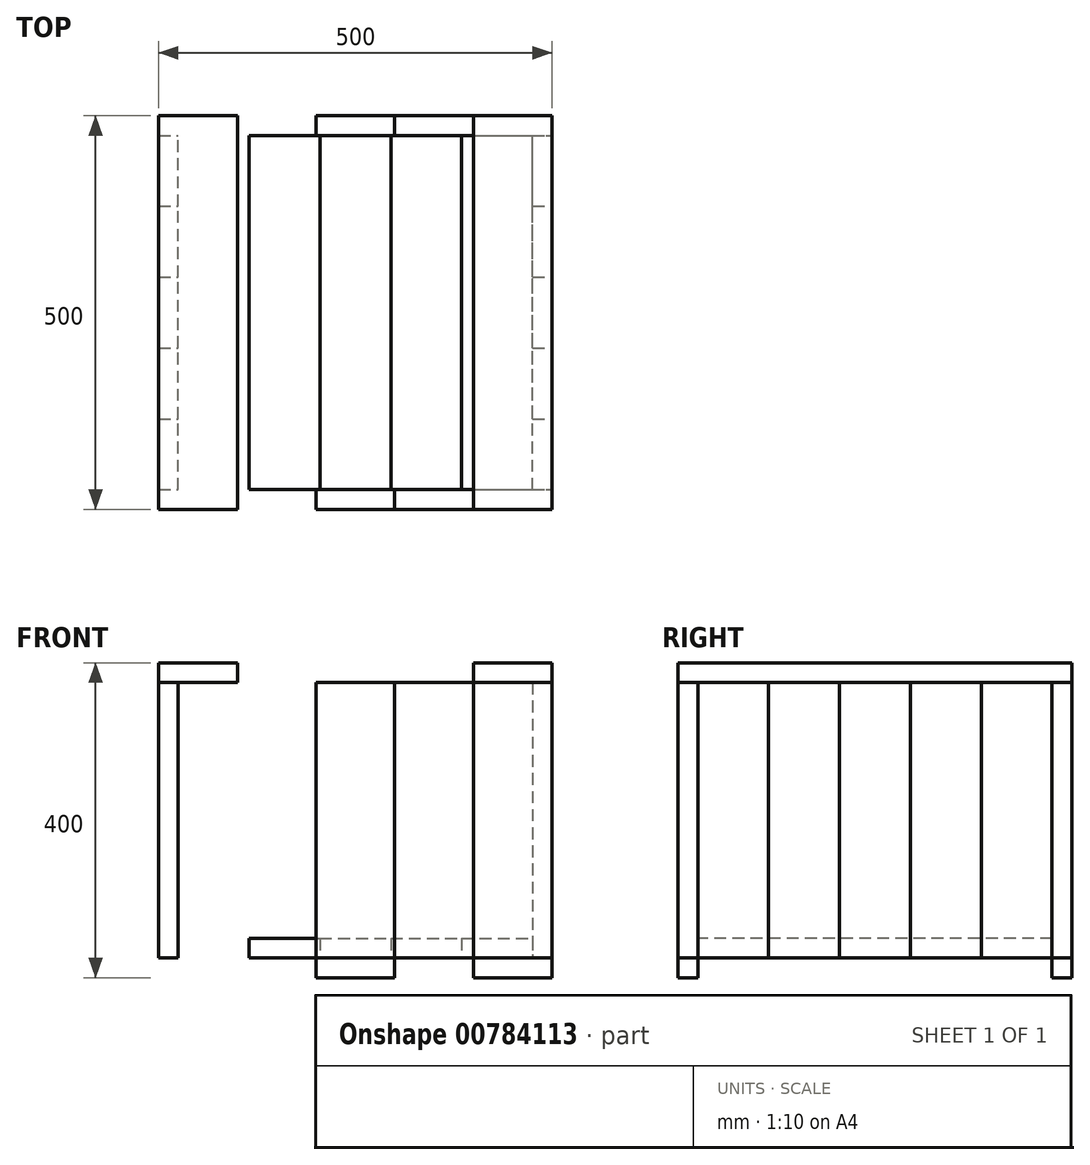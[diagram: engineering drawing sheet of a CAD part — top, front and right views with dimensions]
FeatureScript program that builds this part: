
annotation { "Feature Type Name" : "Feature", "Feature Type Description" : "" }
export const myFeature = defineFeature(function(context is Context, id is Id, definition is map)
    precondition{}
    {
        {
            var Q0;
            Q0=qCreatedBy(makeId("Top.planeOp"),FACE);
            var sketch = newSketch(context, id + "F0", { "sketchPlane" : qUnion([Q0])});
            skLineSegment(sketch, "E0.bottom", {"start": v(0, 0) * mm, "end": v(450, 0) * mm});
            skLineSegment(sketch, "E0.top", {"start": v(0, 450) * mm, "end": v(450, 450) * mm});
            skLineSegment(sketch, "E0.left", {"start": v(0, 0) * mm, "end": v(0, 450) * mm});
            skLineSegment(sketch, "E0.right", {"start": v(450, 0) * mm, "end": v(450, 450) * mm});
            skLineSegment(sketch, "E1.bottom", {"start": v(0, 450) * mm, "end": v(90, 450) * mm});
            skLineSegment(sketch, "E1.top", {"start": v(0, 0) * mm, "end": v(90, 0) * mm});
            skLineSegment(sketch, "E1.left", {"start": v(0, 450) * mm, "end": v(0, 0) * mm});
            skLineSegment(sketch, "E1.right", {"start": v(90, 450) * mm, "end": v(90, 0) * mm});
            skLineSegment(sketch, "E2.1.0.0", {"start": v(180, 450) * mm, "end": v(180, 0) * mm});
            skLineSegment(sketch, "E2.2.0.0", {"start": v(270, 450) * mm, "end": v(270, 0) * mm});
            skLineSegment(sketch, "E2.3.0.0", {"start": v(360, 450) * mm, "end": v(360, 0) * mm});
            skLineSegment(sketch, "E2.direction1", {"start": v(90, 0) * mm, "end": v(180, 0) * mm, "construction": true});
            skLineSegment(sketch, "E3.0", {"start": v(-25, 475) * mm, "end": v(475, 475) * mm});
            skLineSegment(sketch, "E3.1", {"start": v(-25, 475) * mm, "end": v(-25, -25) * mm});
            skLineSegment(sketch, "E3.2", {"start": v(-25, -25) * mm, "end": v(475, -25) * mm});
            skLineSegment(sketch, "E3.3", {"start": v(475, -25) * mm, "end": v(475, 475) * mm});
            skLineSegment(sketch, "E4.bottom", {"start": v(-25, -25) * mm, "end": v(75, -25) * mm});
            skLineSegment(sketch, "E4.top", {"start": v(-25, 0) * mm, "end": v(75, 0) * mm});
            skLineSegment(sketch, "E4.left", {"start": v(-25, -25) * mm, "end": v(-25, 0) * mm});
            skLineSegment(sketch, "E4.right", {"start": v(75, -25) * mm, "end": v(75, 0) * mm});
            skLineSegment(sketch, "E5.1.0.0", {"start": v(175, -25) * mm, "end": v(175, 0) * mm});
            skLineSegment(sketch, "E5.2.0.0", {"start": v(275, -25) * mm, "end": v(275, 0) * mm});
            skLineSegment(sketch, "E5.3.0.0", {"start": v(375, -25) * mm, "end": v(375, 0) * mm});
            skLineSegment(sketch, "E5.direction1", {"start": v(75, -25) * mm, "end": v(175, -25) * mm, "construction": true});
            skLineSegment(sketch, "E6", {"start": v(450, 0) * mm, "end": v(475, 0) * mm});
            skLineSegment(sketch, "E7", {"start": v(450, 90) * mm, "end": v(475, 90) * mm});
            skLineSegment(sketch, "E8.0.1.0", {"start": v(450, 180) * mm, "end": v(475, 180) * mm});
            skLineSegment(sketch, "E8.0.2.0", {"start": v(450, 270) * mm, "end": v(475, 270) * mm});
            skLineSegment(sketch, "E8.0.3.0", {"start": v(450, 360) * mm, "end": v(475, 360) * mm});
            skLineSegment(sketch, "E8.direction1", {"start": v(450, 90) * mm, "end": v(475, 90) * mm, "construction": true});
            skLineSegment(sketch, "E8.direction2", {"start": v(450, 90) * mm, "end": v(450, 180) * mm, "construction": true});
            skLineSegment(sketch, "E9", {"start": v(450, 450) * mm, "end": v(475, 450) * mm});
            skSolve(sketch);
        }
        {
            var Q0;
            Q0=makeQuery(id+"F0.imprint","IMPRINT",FACE,{"disambiguationData":[TD([[makeQuery(id+"F0.imprint","IMPRINT",EDGE,{"derivedFrom":sQuery(id+"F0.wireOp",EDGE,"E1.bottom")}),-1.0]])]});
            var Q1;
            {var subQ0=sQuery(id+"F0.wireOp",EDGE,"E2.1.0.0");Q1=makeQuery(id+"F0.imprint","IMPRINT",FACE,{"disambiguationData":[TD([[makeQuery(id+"F0.imprint","IMPRINT",EDGE,{"derivedFrom":subQ0}),1.0]])]});}
            var Q2;
            {var subQ0=sQuery(id+"F0.wireOp",EDGE,"E0.right");Q2=makeQuery(id+"F0.imprint","IMPRINT",FACE,{"disambiguationData":[TD([[makeQuery(id+"F0.imprint","IMPRINT",EDGE,{"derivedFrom":subQ0}),1.0]])]});}
            extrude(context, id + "F1", {"entities" : qUnion([Q0, Q1, Q2]), "depth" : 25 * mm, "offsetDistance" : 25 * mm});
        }
        {
            var Q0;
            {var subQ0=sQuery(id+"F0.wireOp",EDGE,"E1.right");Q0=makeQuery(id+"F0.imprint","IMPRINT",FACE,{"disambiguationData":[TD([[makeQuery(id+"F0.imprint","IMPRINT",EDGE,{"derivedFrom":subQ0}),1.0]])]});}
            var Q1;
            {var subQ0=sQuery(id+"F0.wireOp",EDGE,"E2.2.0.0");Q1=makeQuery(id+"F0.imprint","IMPRINT",FACE,{"disambiguationData":[TD([[makeQuery(id+"F0.imprint","IMPRINT",EDGE,{"derivedFrom":subQ0}),1.0]])]});}
            extrude(context, id + "F2", {"entities" : qUnion([Q0, Q1]), "depth" : 25 * mm, "offsetDistance" : 25 * mm});
        }
        {
            var Q0;
            Q0=makeQuery(id+"F0.imprint","IMPRINT",FACE,{"disambiguationData":[TD([[makeQuery(id+"F0.imprint","IMPRINT",EDGE,{"derivedFrom":sQuery(id+"F0.wireOp",EDGE,"E4.bottom")}),1.0]])]});
            var Q1;
            {var subQ3=sQuery(id+"F0.wireOp",EDGE,"E5.1.0.0");Q1=makeQuery(id+"F0.imprint","IMPRINT",FACE,{"disambiguationData":[TD([[makeQuery(id+"F0.imprint","IMPRINT",EDGE,{"derivedFrom":subQ3}),-1.0]])]});}
            var Q2;
            {var subQ4=sQuery(id+"F0.wireOp",EDGE,"E5.3.0.0");Q2=makeQuery(id+"F0.imprint","IMPRINT",FACE,{"disambiguationData":[TD([[makeQuery(id+"F0.imprint","IMPRINT",EDGE,{"derivedFrom":subQ4}),-1.0]])]});}
            extrude(context, id + "F3", {"entities" : qUnion([Q0, Q1, Q2]), "depth" : 350 * mm, "offsetDistance" : 25 * mm});
        }
        {
            var Q0;
            {var subQ3=sQuery(id+"F0.wireOp",EDGE,"E1.top");Q0=makeQuery(id+"F0.imprint","IMPRINT",FACE,{"disambiguationData":[TD([[makeQuery(id+"F0.imprint","IMPRINT",EDGE,{"derivedFrom":subQ3}),-1.0]])]});}
            var Q1;
            {var subQ0=sQuery(id+"F0.wireOp",EDGE,"E5.2.0.0");Q1=makeQuery(id+"F0.imprint","IMPRINT",FACE,{"disambiguationData":[TD([[makeQuery(id+"F0.imprint","IMPRINT",EDGE,{"derivedFrom":subQ0}),-1.0]])]});}
            extrude(context, id + "F4", {"entities" : qUnion([Q0, Q1]), "depth" : 350 * mm, "offsetDistance" : 25 * mm});
        }
        {
            var Q0;
            Q0=makeQuery(id+"F3.opExtrude","SWEPT_BODY",BODY,{"disambiguationData":[OSD([sQuery(id+"F0.wireOp",EDGE,"E4.bottom"),sQuery(id+"F0.wireOp",EDGE,"E4.top"),sQuery(id+"F0.wireOp",EDGE,"E4.left"),sQuery(id+"F0.wireOp",EDGE,"E4.right")])]});
            var Q1;
            Q1=makeQuery(id+"F4.opExtrude","SWEPT_BODY",BODY,{"disambiguationData":[OSD([sQuery(id+"F0.wireOp",EDGE,"E0.bottom"),sQuery(id+"F0.wireOp",EDGE,"E1.top"),sQuery(id+"F0.wireOp",EDGE,"E3.2"),sQuery(id+"F0.wireOp",EDGE,"E4.right"),sQuery(id+"F0.wireOp",EDGE,"E5.1.0.0")])]});
            var Q2;
            Q2=makeQuery(id+"F3.opExtrude","SWEPT_BODY",BODY,{"disambiguationData":[OSD([sQuery(id+"F0.wireOp",EDGE,"E0.bottom"),sQuery(id+"F0.wireOp",EDGE,"E3.2"),sQuery(id+"F0.wireOp",EDGE,"E5.1.0.0"),sQuery(id+"F0.wireOp",EDGE,"E5.2.0.0")])]});
            var Q3;
            Q3=makeQuery(id+"F4.opExtrude","SWEPT_BODY",BODY,{"disambiguationData":[OSD([sQuery(id+"F0.wireOp",EDGE,"E0.bottom"),sQuery(id+"F0.wireOp",EDGE,"E3.2"),sQuery(id+"F0.wireOp",EDGE,"E5.2.0.0"),sQuery(id+"F0.wireOp",EDGE,"E5.3.0.0")])]});
            var Q4;
            Q4=makeQuery(id+"F3.opExtrude","SWEPT_BODY",BODY,{"disambiguationData":[OSD([sQuery(id+"F0.wireOp",EDGE,"E0.bottom"),sQuery(id+"F0.wireOp",EDGE,"E3.2"),sQuery(id+"F0.wireOp",EDGE,"E3.3"),sQuery(id+"F0.wireOp",EDGE,"E5.3.0.0"),sQuery(id+"F0.wireOp",EDGE,"E6")])]});
            var Q5;
            Q5=makeQuery(id+"F3.opExtrude","SWEPT_FACE",FACE,{"disambiguationData":[OSD([sQuery(id+"F0.wireOp",EDGE,"E0.bottom")])]});
            transform(context, id + "F5", {"entities" : qUnion([Q0, Q1, Q2, Q3, Q4]), "transformType" : TransformType.TRANSLATION_DISTANCE, "transformDirection" : qUnion([Q5]), "distance" : 475 * mm, "makeCopy" : true});
        }
        {
            var Q0;
            Q0=makeQuery(id+"F3.opExtrude","CAP_FACE",FACE,{"disambiguationData":[OSD([sQuery(id+"F0.wireOp",EDGE,"E4.bottom"),sQuery(id+"F0.wireOp",EDGE,"E4.top"),sQuery(id+"F0.wireOp",EDGE,"E4.left"),sQuery(id+"F0.wireOp",EDGE,"E4.right")])],"isStart":true});
            var Q1;
            Q1=makeQuery(id+"F3.opExtrude","CAP_FACE",FACE,{"disambiguationData":[OSD([sQuery(id+"F0.wireOp",EDGE,"E0.bottom"),sQuery(id+"F0.wireOp",EDGE,"E3.2"),sQuery(id+"F0.wireOp",EDGE,"E5.1.0.0"),sQuery(id+"F0.wireOp",EDGE,"E5.2.0.0")])],"isStart":true});
            var Q2;
            Q2=makeQuery(id+"F3.opExtrude","CAP_FACE",FACE,{"disambiguationData":[OSD([sQuery(id+"F0.wireOp",EDGE,"E0.bottom"),sQuery(id+"F0.wireOp",EDGE,"E3.2"),sQuery(id+"F0.wireOp",EDGE,"E3.3"),sQuery(id+"F0.wireOp",EDGE,"E5.3.0.0"),sQuery(id+"F0.wireOp",EDGE,"E6")])],"isStart":true});
            extrude(context, id + "F6", {"entities" : qUnion([Q0, Q1, Q2]), "depth" : 25 * mm, "offsetDistance" : 25 * mm});
        }
        {
            var Q0;
            Q0=makeQuery(id+"F5.opPattern","COPY",FACE,{"derivedFrom":makeQuery(id+"F3.opExtrude","CAP_FACE",FACE,{"disambiguationData":[OSD([sQuery(id+"F0.wireOp",EDGE,"E0.bottom"),sQuery(id+"F0.wireOp",EDGE,"E3.2"),sQuery(id+"F0.wireOp",EDGE,"E3.3"),sQuery(id+"F0.wireOp",EDGE,"E5.3.0.0"),sQuery(id+"F0.wireOp",EDGE,"E6")])],"isStart":true}),"instanceName":"1"});
            var Q1;
            Q1=makeQuery(id+"F5.opPattern","COPY",FACE,{"derivedFrom":makeQuery(id+"F3.opExtrude","CAP_FACE",FACE,{"disambiguationData":[OSD([sQuery(id+"F0.wireOp",EDGE,"E0.bottom"),sQuery(id+"F0.wireOp",EDGE,"E3.2"),sQuery(id+"F0.wireOp",EDGE,"E5.1.0.0"),sQuery(id+"F0.wireOp",EDGE,"E5.2.0.0")])],"isStart":true}),"instanceName":"1"});
            var Q2;
            Q2=makeQuery(id+"F5.opPattern","COPY",FACE,{"derivedFrom":makeQuery(id+"F3.opExtrude","CAP_FACE",FACE,{"disambiguationData":[OSD([sQuery(id+"F0.wireOp",EDGE,"E4.bottom"),sQuery(id+"F0.wireOp",EDGE,"E4.top"),sQuery(id+"F0.wireOp",EDGE,"E4.left"),sQuery(id+"F0.wireOp",EDGE,"E4.right")])],"isStart":true}),"instanceName":"1"});
            extrude(context, id + "F7", {"entities" : qUnion([Q0, Q1, Q2]), "depth" : 25 * mm, "offsetDistance" : 25 * mm});
        }
        {
            var Q0;
            {var subQ0=sQuery(id+"F0.wireOp",EDGE,"E6");Q0=makeQuery(id+"F0.imprint","IMPRINT",FACE,{"disambiguationData":[TD([[makeQuery(id+"F0.imprint","IMPRINT",EDGE,{"derivedFrom":subQ0}),1.0]])]});}
            var Q1;
            {var subQ0=sQuery(id+"F0.wireOp",EDGE,"E8.0.1.0");Q1=makeQuery(id+"F0.imprint","IMPRINT",FACE,{"disambiguationData":[TD([[makeQuery(id+"F0.imprint","IMPRINT",EDGE,{"derivedFrom":subQ0}),1.0]])]});}
            var Q2;
            {var subQ2=sQuery(id+"F0.wireOp",EDGE,"E8.0.3.0");Q2=makeQuery(id+"F0.imprint","IMPRINT",FACE,{"disambiguationData":[TD([[makeQuery(id+"F0.imprint","IMPRINT",EDGE,{"derivedFrom":subQ2}),1.0]])]});}
            extrude(context, id + "F8", {"entities" : qUnion([Q0, Q1, Q2]), "depth" : 350 * mm, "offsetDistance" : 25 * mm});
        }
        {
            var Q0;
            {var subQ0=sQuery(id+"F0.wireOp",EDGE,"E7");Q0=makeQuery(id+"F0.imprint","IMPRINT",FACE,{"disambiguationData":[TD([[makeQuery(id+"F0.imprint","IMPRINT",EDGE,{"derivedFrom":subQ0}),1.0]])]});}
            var Q1;
            {var subQ0=sQuery(id+"F0.wireOp",EDGE,"E8.0.2.0");Q1=makeQuery(id+"F0.imprint","IMPRINT",FACE,{"disambiguationData":[TD([[makeQuery(id+"F0.imprint","IMPRINT",EDGE,{"derivedFrom":subQ0}),1.0]])]});}
            extrude(context, id + "F9", {"entities" : qUnion([Q0, Q1]), "depth" : 350 * mm, "offsetDistance" : 25 * mm});
        }
        {
            var Q0;
            Q0=makeQuery(id+"F8.opExtrude","SWEPT_BODY",BODY,{"disambiguationData":[OSD([sQuery(id+"F0.wireOp",EDGE,"E0.right"),sQuery(id+"F0.wireOp",EDGE,"E3.3"),sQuery(id+"F0.wireOp",EDGE,"E8.0.3.0"),sQuery(id+"F0.wireOp",EDGE,"E9")])]});
            var Q1;
            Q1=makeQuery(id+"F9.opExtrude","SWEPT_BODY",BODY,{"disambiguationData":[OSD([sQuery(id+"F0.wireOp",EDGE,"E0.right"),sQuery(id+"F0.wireOp",EDGE,"E3.3"),sQuery(id+"F0.wireOp",EDGE,"E8.0.2.0"),sQuery(id+"F0.wireOp",EDGE,"E8.0.3.0")])]});
            var Q2;
            Q2=makeQuery(id+"F8.opExtrude","SWEPT_BODY",BODY,{"disambiguationData":[OSD([sQuery(id+"F0.wireOp",EDGE,"E0.right"),sQuery(id+"F0.wireOp",EDGE,"E3.3"),sQuery(id+"F0.wireOp",EDGE,"E8.0.1.0"),sQuery(id+"F0.wireOp",EDGE,"E8.0.2.0")])]});
            var Q3;
            Q3=makeQuery(id+"F9.opExtrude","SWEPT_BODY",BODY,{"disambiguationData":[OSD([sQuery(id+"F0.wireOp",EDGE,"E0.right"),sQuery(id+"F0.wireOp",EDGE,"E3.3"),sQuery(id+"F0.wireOp",EDGE,"E7"),sQuery(id+"F0.wireOp",EDGE,"E8.0.1.0")])]});
            var Q4;
            Q4=makeQuery(id+"F8.opExtrude","SWEPT_BODY",BODY,{"disambiguationData":[OSD([sQuery(id+"F0.wireOp",EDGE,"E0.right"),sQuery(id+"F0.wireOp",EDGE,"E3.3"),sQuery(id+"F0.wireOp",EDGE,"E6"),sQuery(id+"F0.wireOp",EDGE,"E7")])]});
            var Q5;
            {var subQ0=sQuery(id+"F0.wireOp",EDGE,"E0.right");Q5=makeQuery(id+"F9.opExtrude","SWEPT_FACE",FACE,{"disambiguationData":[OSD([subQ0]),TDD([makeQuery(id+"F0.imprint","IMPRINT",EDGE,{"disambiguationData":[TD([[makeQuery(id+"F0.imprint","INTERSECT",VERTEX,{"derivedFrom":[subQ0,sQuery(id+"F0.wireOp",EDGE,"E8.0.2.0")]}),-1.0]])],"derivedFrom":subQ0})])]});}
            transform(context, id + "F10", {"entities" : qUnion([Q0, Q1, Q2, Q3, Q4]), "transformType" : TransformType.TRANSLATION_DISTANCE, "transformDirection" : qUnion([Q5]), "distance" : 475 * mm, "makeCopy" : true});
        }
        {
            var Q0;
            Q0=makeQuery(id+"F5.opPattern","COPY",FACE,{"derivedFrom":makeQuery(id+"F3.opExtrude","CAP_FACE",FACE,{"disambiguationData":[OSD([sQuery(id+"F0.wireOp",EDGE,"E0.bottom"),sQuery(id+"F0.wireOp",EDGE,"E3.2"),sQuery(id+"F0.wireOp",EDGE,"E3.3"),sQuery(id+"F0.wireOp",EDGE,"E5.3.0.0"),sQuery(id+"F0.wireOp",EDGE,"E6")])],"isStart":false}),"instanceName":"1"});
            var sketch = newSketch(context, id + "F11", { "sketchPlane" : qUnion([Q0])});
            skLineSegment(sketch, "E10.bottom", {"start": v(475, 475) * mm, "end": v(375, 475) * mm});
            skLineSegment(sketch, "E10.top", {"start": v(475, -25) * mm, "end": v(375, -25) * mm});
            skLineSegment(sketch, "E10.left", {"start": v(475, 475) * mm, "end": v(475, -25) * mm});
            skLineSegment(sketch, "E10.right", {"start": v(375, 475) * mm, "end": v(375, -25) * mm});
            skLineSegment(sketch, "E11.bottom", {"start": v(-25, 475) * mm, "end": v(75, 475) * mm});
            skLineSegment(sketch, "E11.top", {"start": v(-25, -25) * mm, "end": v(75, -25) * mm});
            skLineSegment(sketch, "E11.left", {"start": v(-25, 475) * mm, "end": v(-25, -25) * mm});
            skLineSegment(sketch, "E11.right", {"start": v(75, 475) * mm, "end": v(75, -25) * mm});
            skSolve(sketch);
        }
        {
            var Q0;
            {var subQ0=sQuery(id+"F11.wireOp",EDGE,"E10.top");Q0=makeQuery(id+"F11.imprint","IMPRINT",FACE,{"disambiguationData":[TD([[makeQuery(id+"F11.imprint","IMPRINT",EDGE,{"derivedFrom":subQ0}),-1.0]])]});}
            var Q1;
            {var subQ0=sQuery(id+"F11.wireOp",EDGE,"E10.bottom");Q1=makeQuery(id+"F11.imprint","IMPRINT",FACE,{"disambiguationData":[TD([[makeQuery(id+"F11.imprint","IMPRINT",EDGE,{"derivedFrom":subQ0}),-1.0]])]});}
            var Q2;
            Q2=makeQuery(id+"F11.imprint","IMPRINT",FACE,{"disambiguationData":[TD([[makeQuery(id+"F11.imprint","IMPRINT",EDGE,{"derivedFrom":sQuery(id+"F11.wireOp",EDGE,"E11.bottom")}),-1.0]])]});
            extrude(context, id + "F12", {"entities" : qUnion([Q0, Q1, Q2]), "depth" : 25 * mm, "offsetDistance" : 25 * mm});
        }
    });
